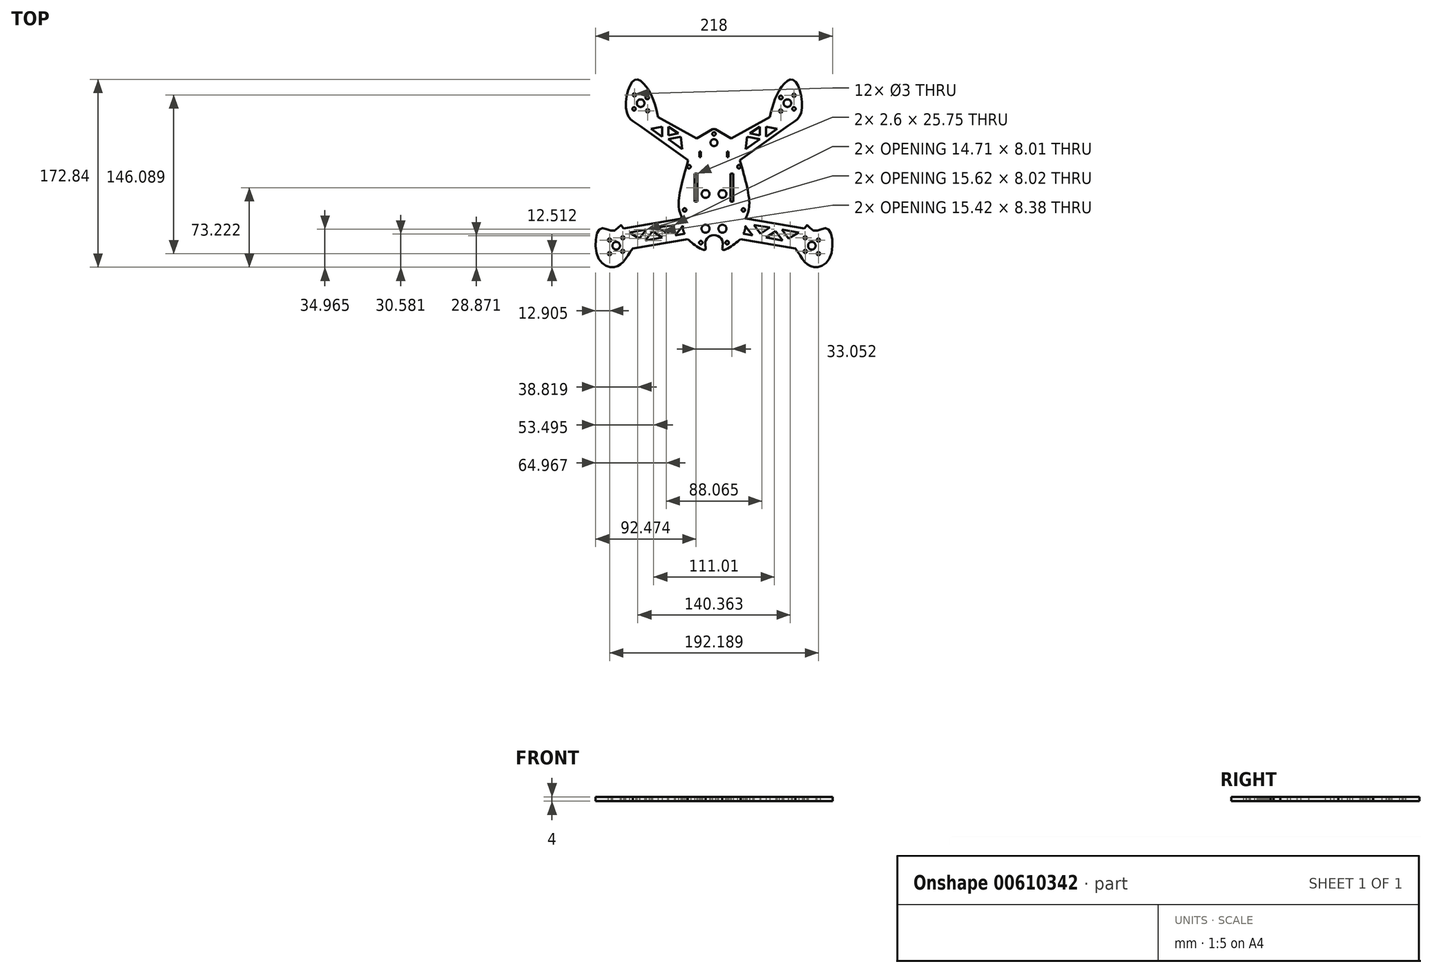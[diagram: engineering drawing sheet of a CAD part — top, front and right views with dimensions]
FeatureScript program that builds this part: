
annotation { "Feature Type Name" : "Feature", "Feature Type Description" : "" }
export const myFeature = defineFeature(function(context is Context, id is Id, definition is map)
    precondition{}
    {
        {
            var Q0;
            Q0=qCreatedBy(makeId("Top.planeOp"),FACE);
            var sketch = newSketch(context, id + "F0", { "sketchPlane" : qUnion([Q0])});
            skCircle(sketch, "E0", {"center": v(-90, -29.8) * mm, "radius": 3.5 * mm});
            skCircle(sketch, "E1", {"center": v(-96.1, -37.08) * mm, "radius": 1.5 * mm});
            skCircle(sketch, "E2", {"center": v(-83.9, -22.5) * mm, "radius": 1.5 * mm});
            skCircle(sketch, "E3", {"center": v(-96.07, -24.58) * mm, "radius": 1.5 * mm});
            skCircle(sketch, "E4", {"center": v(-83.93, -35) * mm, "radius": 1.5 * mm});
            skCircle(sketch, "E5.MirrorC", {"center": v(96.1, -37.08) * mm, "radius": 1.5 * mm});
            skCircle(sketch, "E6.MirrorC", {"center": v(83.93, -35) * mm, "radius": 1.5 * mm});
            skCircle(sketch, "E7.MirrorC", {"center": v(83.9, -22.5) * mm, "radius": 1.5 * mm});
            skCircle(sketch, "E8.MirrorC", {"center": v(96.07, -24.58) * mm, "radius": 1.5 * mm});
            skCircle(sketch, "E9.MirrorC", {"center": v(90, -29.8) * mm, "radius": 3.5 * mm});
            skCircle(sketch, "E10", {"center": v(67.5, 101.43) * mm, "radius": 3.5 * mm});
            skCircle(sketch, "E11", {"center": v(61.4, 94.14) * mm, "radius": 1.5 * mm});
            skCircle(sketch, "E12", {"center": v(73.6, 108.72) * mm, "radius": 1.5 * mm});
            skCircle(sketch, "E13", {"center": v(61.43, 106.64) * mm, "radius": 1.65 * mm});
            skCircle(sketch, "E14", {"center": v(73.57, 96.22) * mm, "radius": 1.54 * mm});
            skCircle(sketch, "E15.MirrorC", {"center": v(-61.05, 94.45) * mm, "radius": 1.5 * mm});
            skCircle(sketch, "E16.MirrorC", {"center": v(-73.52, 96.17) * mm, "radius": 1.54 * mm});
            skCircle(sketch, "E17.MirrorC", {"center": v(-73.22, 109.01) * mm, "radius": 1.5 * mm});
            skCircle(sketch, "E18.MirrorC", {"center": v(-61.43, 106.64) * mm, "radius": 1.65 * mm});
            skCircle(sketch, "E19.MirrorC", {"center": v(-67.5, 101.43) * mm, "radius": 3.5 * mm});
            skLineSegment(sketch, "E20", {"start": v(-83.26, -13.8) * mm, "end": v(-29.18, -4.57) * mm});
            skLineSegment(sketch, "E21", {"start": v(-74.8, -32.33) * mm, "end": v(-24.23, -23.7) * mm});
            skLineSegment(sketch, "E22.MirrorCS", {"start": v(83.26, -13.8) * mm, "end": v(29.18, -4.57) * mm});
            skLineSegment(sketch, "E23.MirrorCS", {"start": v(74.8, -32.33) * mm, "end": v(24.23, -23.7) * mm});
            skFitSpline(sketch, "E24", {"points": [v(83.26, -13.8) * mm, v(90.69, -15.53) * mm, v(104, -13.8) * mm, v(106.85, -40.28) * mm, v(92.32, -49.56) * mm, v(83.26, -44.36) * mm, v(74.8, -32.33) * mm], "startDerivative": vector(48.4, 165.36) * mm, "endDerivative": vector(-54.7, 69.22) * mm});
            skFitSpline(sketch, "E25.MirrorCS", {"points": [v(-83.26, -13.8) * mm, v(-90.69, -15.53) * mm, v(-104, -13.8) * mm, v(-106.85, -40.28) * mm, v(-92.32, -49.56) * mm, v(-83.26, -44.36) * mm, v(-74.8, -32.33) * mm], "startDerivative": vector(-48.4, 165.36) * mm, "endDerivative": vector(54.7, 69.22) * mm});
            skLineSegment(sketch, "E26", {"start": v(-68.28, 80.75) * mm, "end": v(-23.77, 48.85) * mm});
            skLineSegment(sketch, "E27", {"start": v(-51.38, 88.72) * mm, "end": v(-15.87, 68.91) * mm});
            skFitSpline(sketch, "E28", {"points": [v(-68.28, 80.75) * mm, v(-80.38, 93.36) * mm, v(-73.14, 122.75) * mm, v(-60.82, 114.46) * mm, v(-51.38, 88.72) * mm], "startDerivative": vector(-63.76, 40.55) * mm, "endDerivative": vector(23.21, -100.38) * mm});
            skLineSegment(sketch, "E29.MirrorCS", {"start": v(51.38, 88.72) * mm, "end": v(15.87, 68.91) * mm});
            skLineSegment(sketch, "E30.MirrorCS", {"start": v(68.28, 80.75) * mm, "end": v(23.77, 48.85) * mm});
            skFitSpline(sketch, "E31.MirrorCS", {"points": [v(68.28, 80.75) * mm, v(80.38, 93.36) * mm, v(73.14, 122.75) * mm, v(60.82, 114.46) * mm, v(51.38, 88.72) * mm], "startDerivative": vector(63.76, 40.55) * mm, "endDerivative": vector(-23.21, -100.38) * mm});
            skFitSpline(sketch, "E32", {"points": [v(-29.18, -4.57) * mm, v(-32.5, 7.93) * mm, v(-23.77, 48.85) * mm], "startDerivative": vector(-13.42, 29.87) * mm, "endDerivative": vector(20.99, 72.88) * mm});
            skLineSegment(sketch, "E33", {"start": v(-15.87, 68.91) * mm, "end": v(-1.3, 77.4) * mm});
            skLineSegment(sketch, "E34", {"start": v(-1.3, 77.4) * mm, "end": v(0, 77.4) * mm});
            skLineSegment(sketch, "E35.MirrorCS", {"start": v(15.87, 68.91) * mm, "end": v(1.3, 77.4) * mm});
            skLineSegment(sketch, "E36.MirrorCS", {"start": v(1.3, 77.4) * mm, "end": v(0, 77.4) * mm});
            skFitSpline(sketch, "E37.MirrorCS", {"points": [v(29.18, -4.57) * mm, v(32.5, 7.93) * mm, v(23.77, 48.85) * mm], "startDerivative": vector(13.42, 29.87) * mm, "endDerivative": vector(-20.99, 72.88) * mm});
            skFitSpline(sketch, "E38", {"points": [v(-24.23, -23.7) * mm, v(-15.08, -30.83) * mm, v(-8, -33.43) * mm, v(-8, -26.5) * mm, v(0, -20.01) * mm], "startDerivative": vector(27.48, -26.26) * mm, "endDerivative": vector(47.09, 0) * mm});
            skFitSpline(sketch, "E39.MirrorCS", {"points": [v(24.23, -23.7) * mm, v(15.08, -30.83) * mm, v(8, -33.43) * mm, v(8, -26.5) * mm, v(0, -20.01) * mm], "startDerivative": vector(-27.48, -26.26) * mm, "endDerivative": vector(-47.09, 0) * mm});
            skCircle(sketch, "E40", {"center": v(-12.12, -26.95) * mm, "radius": 1.56 * mm});
            skCircle(sketch, "E41", {"center": v(-27.03, 3.13) * mm, "radius": 1.56 * mm});
            skCircle(sketch, "E42", {"center": v(-22.94, 42.94) * mm, "radius": 1.58 * mm});
            skCircle(sketch, "E43", {"center": v(0, 73.16) * mm, "radius": 1.56 * mm});
            skPoint(sketch, "E43.centerSnap0", {"position": v(-8.58, 73.16) * mm});
            skLineSegment(sketch, "E44", {"start": v(-15.23, 17.22) * mm, "end": v(-15.23, 36.5) * mm});
            skLineSegment(sketch, "E45", {"start": v(-15.23, 36.5) * mm, "end": v(-17.82, 36.5) * mm});
            skLineSegment(sketch, "E46", {"start": v(-17.82, 36.5) * mm, "end": v(-17.82, 10.76) * mm});
            skLineSegment(sketch, "E47", {"start": v(-17.82, 10.76) * mm, "end": v(-15.23, 10.76) * mm});
            skLineSegment(sketch, "E48", {"start": v(-15.23, 10.76) * mm, "end": v(-15.23, 17.22) * mm});
            skLineSegment(sketch, "E49.MirrorCS", {"start": v(15.23, 17.22) * mm, "end": v(15.23, 36.5) * mm});
            skLineSegment(sketch, "E50.MirrorCS", {"start": v(15.23, 10.76) * mm, "end": v(15.23, 17.22) * mm});
            skLineSegment(sketch, "E51.MirrorCS", {"start": v(17.82, 36.5) * mm, "end": v(17.82, 10.76) * mm});
            skLineSegment(sketch, "E52.MirrorCS", {"start": v(15.23, 36.5) * mm, "end": v(17.82, 36.5) * mm});
            skLineSegment(sketch, "E53.MirrorCS", {"start": v(17.82, 10.76) * mm, "end": v(15.23, 10.76) * mm});
            skCircle(sketch, "E54.MirrorC", {"center": v(27.03, 3.13) * mm, "radius": 1.56 * mm});
            skCircle(sketch, "E55.MirrorC", {"center": v(22.94, 42.94) * mm, "radius": 1.58 * mm});
            skCircle(sketch, "E56.MirrorC", {"center": v(12.12, -26.95) * mm, "radius": 1.56 * mm});
            skLineSegment(sketch, "E57", {"start": v(-78, -17.66) * mm, "end": v(-68.66, -23.02) * mm});
            skLineSegment(sketch, "E58", {"start": v(-68.66, -23.02) * mm, "end": v(-62.37, -15) * mm});
            skLineSegment(sketch, "E59", {"start": v(-63.22, -24.91) * mm, "end": v(-56.64, -16.53) * mm});
            skLineSegment(sketch, "E60", {"start": v(-56.64, -16.53) * mm, "end": v(-47.8, -22.28) * mm});
            skLineSegment(sketch, "E61", {"start": v(-51.39, -13.13) * mm, "end": v(-42.93, -18.63) * mm});
            skLineSegment(sketch, "E62", {"start": v(-42.93, -18.63) * mm, "end": v(-36.68, -10.62) * mm});
            skLineSegment(sketch, "E63", {"start": v(-35.6, -20.2) * mm, "end": v(-28.66, -11.31) * mm});
            skFitSpline(sketch, "E64", {"points": [v(-28.66, -11.31) * mm, v(-28.66, -14.3) * mm, v(-27.03, -18.74) * mm], "startDerivative": vector(-0.77, -9.34) * mm, "endDerivative": vector(3.49, -6.3) * mm});
            skLineSegment(sketch, "E65", {"start": v(-63.22, -24.91) * mm, "end": v(-47.8, -22.28) * mm});
            skLineSegment(sketch, "E66", {"start": v(-35.6, -20.2) * mm, "end": v(-27.03, -18.74) * mm});
            skLineSegment(sketch, "E67", {"start": v(-36.68, -10.62) * mm, "end": v(-51.39, -13.13) * mm});
            skLineSegment(sketch, "E68", {"start": v(-62.37, -15) * mm, "end": v(-78, -17.66) * mm});
            skLineSegment(sketch, "E69.MirrorCS", {"start": v(78, -17.66) * mm, "end": v(68.66, -23.02) * mm});
            skLineSegment(sketch, "E70.MirrorCS", {"start": v(35.6, -20.2) * mm, "end": v(27.03, -18.74) * mm});
            skLineSegment(sketch, "E71.MirrorCS", {"start": v(56.64, -16.53) * mm, "end": v(47.8, -22.28) * mm});
            skLineSegment(sketch, "E72.MirrorCS", {"start": v(42.93, -18.63) * mm, "end": v(36.68, -10.62) * mm});
            skFitSpline(sketch, "E73.MirrorCS", {"points": [v(28.66, -11.31) * mm, v(28.66, -14.3) * mm, v(27.03, -18.74) * mm], "startDerivative": vector(0.77, -9.34) * mm, "endDerivative": vector(-3.49, -6.3) * mm});
            skLineSegment(sketch, "E74.MirrorCS", {"start": v(36.68, -10.62) * mm, "end": v(51.39, -13.13) * mm});
            skLineSegment(sketch, "E75.MirrorCS", {"start": v(62.37, -15) * mm, "end": v(78, -17.66) * mm});
            skLineSegment(sketch, "E76.MirrorCS", {"start": v(51.39, -13.13) * mm, "end": v(42.93, -18.63) * mm});
            skLineSegment(sketch, "E77.MirrorCS", {"start": v(35.6, -20.2) * mm, "end": v(28.66, -11.31) * mm});
            skLineSegment(sketch, "E78.MirrorCS", {"start": v(63.22, -24.91) * mm, "end": v(56.64, -16.53) * mm});
            skLineSegment(sketch, "E79.MirrorCS", {"start": v(63.22, -24.91) * mm, "end": v(47.8, -22.28) * mm});
            skLineSegment(sketch, "E80.MirrorCS", {"start": v(68.66, -23.02) * mm, "end": v(62.37, -15) * mm});
            skLineSegment(sketch, "E81", {"start": v(-57.9, 77.94) * mm, "end": v(-47.73, 70.52) * mm});
            skLineSegment(sketch, "E82", {"start": v(-42.05, 68.29) * mm, "end": v(-29.28, 59.13) * mm});
            skLineSegment(sketch, "E83", {"start": v(-57.9, 77.94) * mm, "end": v(-47.73, 79.88) * mm});
            skLineSegment(sketch, "E84", {"start": v(-47.73, 79.88) * mm, "end": v(-47.73, 70.52) * mm});
            skLineSegment(sketch, "E85", {"start": v(-42.05, 68.29) * mm, "end": v(-30.42, 70.52) * mm});
            skLineSegment(sketch, "E86", {"start": v(-30.42, 70.52) * mm, "end": v(-29.28, 59.13) * mm});
            skLineSegment(sketch, "E87", {"start": v(-42.05, 79.67) * mm, "end": v(-32.82, 73.58) * mm});
            skLineSegment(sketch, "E88", {"start": v(-32.82, 73.58) * mm, "end": v(-42.05, 71.8) * mm});
            skLineSegment(sketch, "E89", {"start": v(-42.05, 71.8) * mm, "end": v(-42.05, 79.67) * mm});
            skLineSegment(sketch, "E90.MirrorCS", {"start": v(57.9, 77.94) * mm, "end": v(47.73, 79.88) * mm});
            skLineSegment(sketch, "E91.MirrorCS", {"start": v(57.9, 77.94) * mm, "end": v(47.73, 70.52) * mm});
            skLineSegment(sketch, "E92.MirrorCS", {"start": v(47.73, 79.88) * mm, "end": v(47.73, 70.52) * mm});
            skLineSegment(sketch, "E93.MirrorCS", {"start": v(42.05, 71.8) * mm, "end": v(42.05, 79.67) * mm});
            skLineSegment(sketch, "E94.MirrorCS", {"start": v(42.05, 79.67) * mm, "end": v(32.82, 73.58) * mm});
            skLineSegment(sketch, "E95.MirrorCS", {"start": v(32.82, 73.58) * mm, "end": v(42.05, 71.8) * mm});
            skLineSegment(sketch, "E96.MirrorCS", {"start": v(42.05, 68.29) * mm, "end": v(30.42, 70.52) * mm});
            skLineSegment(sketch, "E97.MirrorCS", {"start": v(42.05, 68.29) * mm, "end": v(29.28, 59.13) * mm});
            skLineSegment(sketch, "E98.MirrorCS", {"start": v(30.42, 70.52) * mm, "end": v(29.28, 59.13) * mm});
            skCircle(sketch, "E99", {"center": v(0, 65.06) * mm, "radius": 3.2 * mm});
            skCircle(sketch, "E100", {"center": v(-7.78, 17.85) * mm, "radius": 3.62 * mm});
            skCircle(sketch, "E101", {"center": v(-7.78, -14.15) * mm, "radius": 3.68 * mm});
            skCircle(sketch, "E102.MirrorC", {"center": v(7.78, 17.85) * mm, "radius": 3.62 * mm});
            skCircle(sketch, "E103.MirrorC", {"center": v(7.78, -14.15) * mm, "radius": 3.68 * mm});
            skLineSegment(sketch, "E104", {"start": v(-13.3, 56.85) * mm, "end": v(-13.3, 51.85) * mm});
            skLineSegment(sketch, "E105", {"start": v(-13.3, 51.85) * mm, "end": v(-12, 51.85) * mm});
            skLineSegment(sketch, "E106", {"start": v(-12, 51.85) * mm, "end": v(-12, 56.85) * mm});
            skLineSegment(sketch, "E107", {"start": v(-12, 56.85) * mm, "end": v(-13.3, 56.85) * mm});
            skLineSegment(sketch, "E108.MirrorCS", {"start": v(12, 56.85) * mm, "end": v(13.3, 56.85) * mm});
            skLineSegment(sketch, "E109.MirrorCS", {"start": v(13.3, 51.85) * mm, "end": v(12, 51.85) * mm});
            skLineSegment(sketch, "E110.MirrorCS", {"start": v(12, 51.85) * mm, "end": v(12, 56.85) * mm});
            skLineSegment(sketch, "E111.MirrorCS", {"start": v(13.3, 56.85) * mm, "end": v(13.3, 51.85) * mm});
            skSolve(sketch);
        }
        {
            var Q0;
            Q0 = qSketchRegion(id + "F0", true);
            extrude(context, id + "F1", {"entities" : qUnion([Q0]), "depth" : 4 * mm, "offsetDistance" : 25 * mm});
        }
    });
